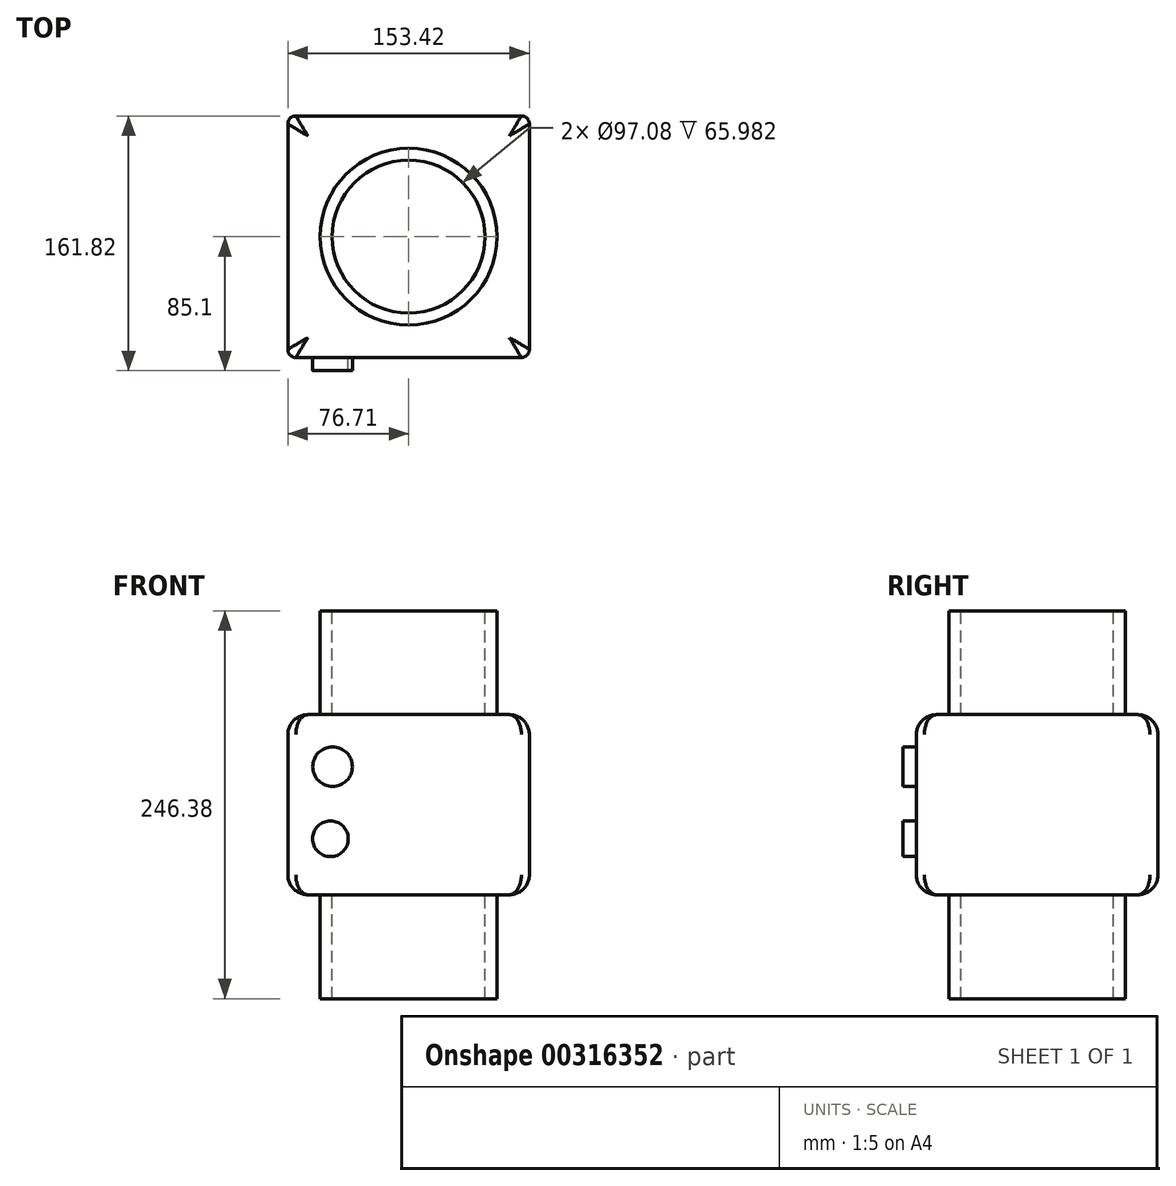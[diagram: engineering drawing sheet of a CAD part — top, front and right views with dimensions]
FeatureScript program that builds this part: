
annotation { "Feature Type Name" : "Feature", "Feature Type Description" : "" }
export const myFeature = defineFeature(function(context is Context, id is Id, definition is map)
    precondition{}
    {
        {
            var Q0;
            Q0=qCreatedBy(makeId("Top.planeOp"),FACE);
            var sketch = newSketch(context, id + "F0", { "sketchPlane" : qUnion([Q0])});
            skCircle(sketch, "E0", {"center": v(0, 0) * mm, "radius": 56.14 * mm});
            skSolve(sketch);
        }
        {
            var Q0;
            Q0=makeQuery(id+"F0.imprint","IMPRINT",FACE,{"disambiguationData":[TD([[makeQuery(id+"F0.imprint","IMPRINT",EDGE,{"derivedFrom":sQuery(id+"F0.wireOp",EDGE,"E0")}),1.0]])]});
            extrude(context, id + "F1", {"entities" : qUnion([Q0]), "endBound" : BoundingType.SYMMETRIC, "depth" : 246.38 * mm});
        }
        {
            var Q0;
            Q0=makeQuery(id+"F1.opExtrude","CAP_FACE",FACE,{"disambiguationData":[OSD([sQuery(id+"F0.wireOp",EDGE,"E0")])],"isStart":false});
            var sketch = newSketch(context, id + "F2", { "sketchPlane" : qUnion([Q0])});
            skCircle(sketch, "E1", {"center": v(0, 0) * mm, "radius": 48.54 * mm});
            skSolve(sketch);
        }
        {
            var Q0;
            Q0 = qSketchRegion(id + "F2", true);
            extrude(context, id + "F3", {"entities" : qUnion([Q0]), "operationType" : NewBodyOperationType.REMOVE, "oppositeDirection" : true, "depth" : 573.02 * mm});
        }
        {
            var Q0;
            Q0=qCreatedBy(makeId("Right.planeOp"),FACE);
            var sketch = newSketch(context, id + "F4", { "sketchPlane" : qUnion([Q0])});
            skLineSegment(sketch, "E2.bottom", {"start": v(76.72, 57.2) * mm, "end": v(-76.72, 57.2) * mm});
            skLineSegment(sketch, "E2.top", {"start": v(76.72, -57.2) * mm, "end": v(-76.72, -57.2) * mm});
            skLineSegment(sketch, "E2.left", {"start": v(76.72, 57.2) * mm, "end": v(76.72, -57.2) * mm});
            skLineSegment(sketch, "E2.right", {"start": v(-76.72, 57.2) * mm, "end": v(-76.72, -57.2) * mm});
            skPoint(sketch, "E2.middle", {"position": v(0, 0) * mm});
            skSolve(sketch);
        }
        {
            var Q0;
            Q0=makeQuery(id+"F4.imprint","IMPRINT",FACE,{"disambiguationData":[TD([[makeQuery(id+"F4.imprint","IMPRINT",EDGE,{"derivedFrom":sQuery(id+"F4.wireOp",EDGE,"E2.bottom")}),1.0]])]});
            extrude(context, id + "F5", {"entities" : qUnion([Q0]), "operationType" : NewBodyOperationType.ADD, "endBound" : BoundingType.SYMMETRIC, "depth" : 153.42 * mm});
        }
        {
            var Q0;
            Q0=makeQuery(id+"F5.opExtrude","CAP_EDGE",EDGE,{"disambiguationData":[OSD([sQuery(id+"F4.wireOp",EDGE,"E2.left")])],"isStart":false});
            var Q1;
            Q1=makeQuery(id+"F5.opExtrude","CAP_EDGE",EDGE,{"disambiguationData":[OSD([sQuery(id+"F4.wireOp",EDGE,"E2.right")])],"isStart":false});
            var Q2;
            Q2=makeQuery(id+"F5.opExtrude","CAP_EDGE",EDGE,{"disambiguationData":[OSD([sQuery(id+"F4.wireOp",EDGE,"E2.left")])],"isStart":true});
            var Q3;
            Q3=makeQuery(id+"F5.opExtrude","CAP_EDGE",EDGE,{"disambiguationData":[OSD([sQuery(id+"F4.wireOp",EDGE,"E2.right")])],"isStart":true});
            fillet(context, id + "F6", {"entities" : qUnion([Q0, Q1, Q2, Q3]), "radius" : 5.08 * mm, "tangentPropagation" : true, "allowEdgeOverflow" : false});
        }
        {
            var Q0;
            Q0=makeQuery(id+"F5.opExtrude","CAP_EDGE",EDGE,{"disambiguationData":[OSD([sQuery(id+"F4.wireOp",EDGE,"E2.bottom")])],"isStart":false});
            var Q1;
            Q1=makeQuery(id+"F5.opExtrude","CAP_EDGE",EDGE,{"disambiguationData":[OSD([sQuery(id+"F4.wireOp",EDGE,"E2.bottom")])],"isStart":true});
            var Q2;
            Q2=makeQuery(id+"F5.opExtrude","CAP_EDGE",EDGE,{"disambiguationData":[OSD([sQuery(id+"F4.wireOp",EDGE,"E2.top")])],"isStart":true});
            var Q3;
            Q3=makeQuery(id+"F5.opExtrude","CAP_EDGE",EDGE,{"disambiguationData":[OSD([sQuery(id+"F4.wireOp",EDGE,"E2.top")])],"isStart":false});
            fillet(context, id + "F7", {"entities" : qUnion([Q0, Q1, Q2, Q3]), "radius" : 12.7 * mm, "tangentPropagation" : true, "allowEdgeOverflow" : false});
        }
        {
            var Q0;
            Q0=makeQuery(id+"F5.opExtrude","SWEPT_FACE",FACE,{"disambiguationData":[OSD([sQuery(id+"F4.wireOp",EDGE,"E2.right")])]});
            var sketch = newSketch(context, id + "F8", { "sketchPlane" : qUnion([Q0])});
            skCircle(sketch, "E3", {"center": v(-48.29, 24.16) * mm, "radius": 12.57 * mm});
            skSolve(sketch);
        }
        {
            var Q0;
            Q0=makeQuery(id+"F5.opExtrude","SWEPT_FACE",FACE,{"disambiguationData":[OSD([sQuery(id+"F4.wireOp",EDGE,"E2.right")])]});
            var sketch = newSketch(context, id + "F9", { "sketchPlane" : qUnion([Q0])});
            skCircle(sketch, "E4", {"center": v(-49.65, -21.6) * mm, "radius": 11.33 * mm});
            skSolve(sketch);
        }
        {
            var Q0;
            Q0 = qSketchRegion(id + "F9", true);
            extrude(context, id + "F10", {"entities" : qUnion([Q0]), "operationType" : NewBodyOperationType.ADD, "depth" : 8.38 * mm});
        }
        {
            var Q0;
            Q0 = qSketchRegion(id + "F8", true);
            extrude(context, id + "F11", {"entities" : qUnion([Q0]), "operationType" : NewBodyOperationType.ADD, "depth" : 8.38 * mm});
        }
    });
